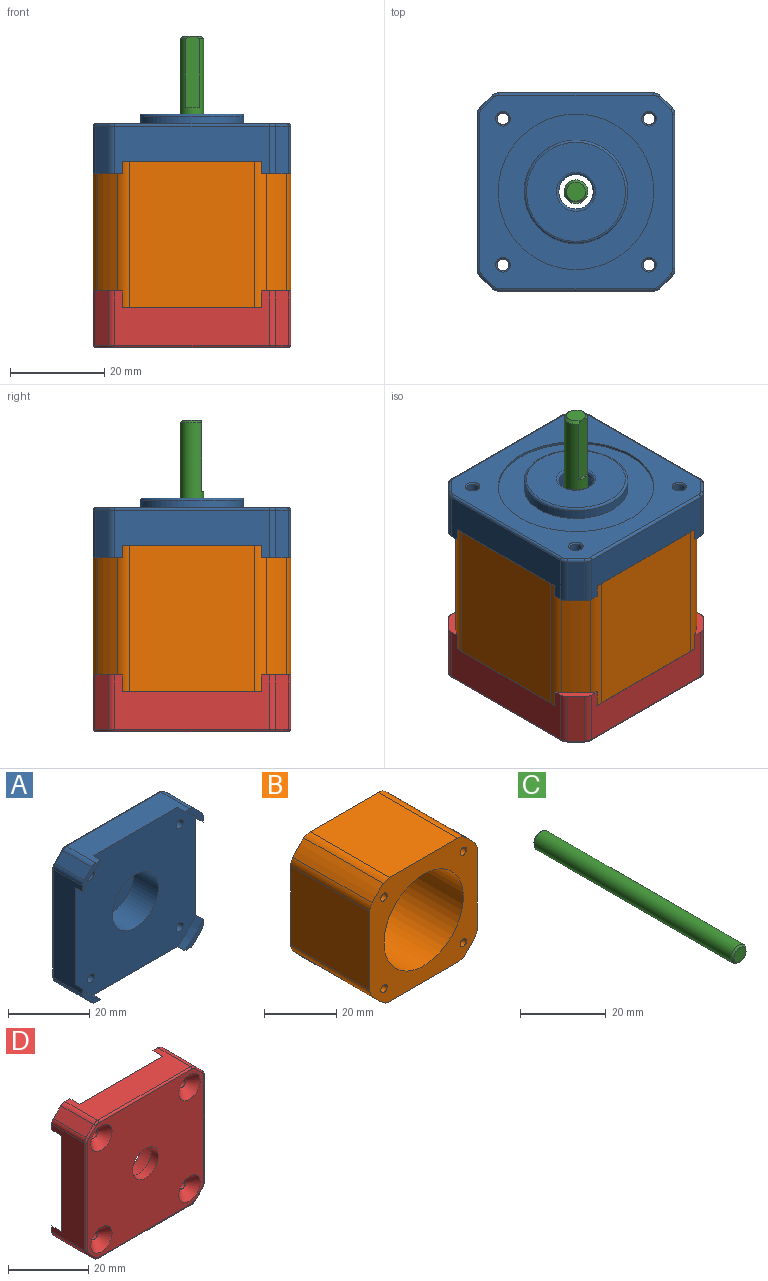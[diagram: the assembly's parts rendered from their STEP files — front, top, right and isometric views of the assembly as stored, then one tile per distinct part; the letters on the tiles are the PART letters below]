
ASSEMBLY  parts=4 mates=3
PART A: 59 faces, bbox 42.3x12.6x42.3 mm
  f0: cylinder r=3.65mm len=7.3mm, axis (0,-1,0), area 20.6mm2, adj f28,f53
  f1: plane 42x42mm, normal (0,-1,0), area 1472mm2, adj f2,f4,f6,f8,f9,f10,f11,f14
  f2: plane 32.74x10.1mm, normal (0,0,1), area 254.6mm2, adj f1,f19,f20,f21,f22,f30,f31,f51
  f3: plane 10.1x2.63mm, normal (0.71,0,0.71), area 37.5mm2, adj f22,f29,f30,f47
  f4: plane 32.74x10.1mm, normal (1,0,0), area 254.6mm2, adj f1,f21,f22,f25,f26,f29,f36,f43
  f5: plane 10.1x2.63mm, normal (0.71,0,-0.71), area 37.5mm2, adj f26,f35,f36,f39
  f6: plane 32.74x10.1mm, normal (0,0,-1), area 254.6mm2, adj f1,f23,f24,f25,f26,f34,f35,f38
  f7: plane 10.1x2.63mm, normal (-0.71,0,-0.71), area 37.5mm2, adj f24,f33,f34,f42
  f8: plane 32.74x10.1mm, normal (-1,0,0), area 254.6mm2, adj f1,f19,f20,f23,f24,f32,f33,f46
  f9: cylinder r=1.25mm len=7.7mm, axis (0,-1,0), area 60.5mm2, adj f1,f58
  f10: cylinder r=1.25mm len=7.7mm, axis (0,-1,0), area 60.5mm2, adj f1,f57
  f11: cylinder r=1.25mm len=7.7mm, axis (0,-1,0), area 60.5mm2, adj f1,f56
  f12: plane 10.1x2.63mm, normal (-0.71,0,0.71), area 37.5mm2, adj f20,f31,f32,f50
  f13: cylinder r=16.5mm len=33mm, axis (0,-1,0), area 51.8mm2, adj f15,f16
  f14: cylinder r=1.25mm len=7.7mm, axis (0,-1,0), area 60.5mm2, adj f1,f55
  f15: plane 41x41mm, normal (0,1,0), area 770.5mm2, adj f13,f37,f38,f39,f40,f41,f42,f43
  f16: plane 33x33mm, normal (0,1,0), area 475.2mm2, adj f13,f17
  f17: cylinder r=11mm len=22mm, axis (0,-1,0), area 138.2mm2, adj f16,f54
  f18: plane 21x21mm, normal (0,1,0), area 292.3mm2, adj f53,f54
  f19: cylinder r=25.6mm len=6.36mm, axis (0,1,0), area 23.5mm2, adj f1,f2,f8,f20
  f20: plane 6.36x6.36mm, normal (0,-1,0), area 10.4mm2, adj f2,f8,f12,f19,f31,f32
  f21: cylinder r=25.6mm len=6.36mm, axis (0,1,0), area 23.5mm2, adj f1,f2,f4,f22
  f22: plane 6.36x6.36mm, normal (0,-1,0), area 10.4mm2, adj f2,f3,f4,f21,f29,f30
  f23: cylinder r=25.6mm len=6.36mm, axis (0,1,0), area 23.5mm2, adj f1,f6,f8,f24
  f24: plane 6.36x6.36mm, normal (0,-1,0), area 10.4mm2, adj f6,f7,f8,f23,f33,f34
  f25: cylinder r=25.6mm len=6.36mm, axis (0,1,0), area 23.5mm2, adj f1,f4,f6,f26
  f26: plane 6.36x6.36mm, normal (0,-1,0), area 10.4mm2, adj f4,f5,f6,f25,f35,f36
  f27: cylinder r=8mm len=16mm, axis (0,-1,0), area 432.3mm2, adj f1,f28
  f28: plane 16x16mm, normal (0,-1,0), area 159.2mm2, adj f0,f27
  f29: cylinder r=2mm len=10.1mm, axis (0,-1,0), area 15.9mm2, adj f3,f4,f22,f45
  f30: cylinder r=2mm len=10.1mm, axis (0,-1,0), area 15.9mm2, adj f2,f3,f22,f49
  f31: cylinder r=2mm len=10.1mm, axis (0,-1,0), area 15.9mm2, adj f2,f12,f20,f52
  f32: cylinder r=2mm len=10.1mm, axis (0,1,0), area 15.9mm2, adj f8,f12,f20,f48
  f33: cylinder r=2mm len=10.1mm, axis (0,-1,0), area 15.9mm2, adj f7,f8,f24,f44
  f34: cylinder r=2mm len=10.1mm, axis (0,-1,0), area 15.9mm2, adj f6,f7,f24,f40
  f35: cylinder r=2mm len=10.1mm, axis (0,-1,0), area 15.9mm2, adj f5,f6,f26,f37
  f36: cylinder r=2mm len=10.1mm, axis (0,1,0), area 15.9mm2, adj f4,f5,f26,f41
  f37: torus R=1.5mm, axis (0,1,0), area 1.1mm2, adj f15,f35,f38,f39
  f38: cylinder r=0.5mm len=32.74mm, axis (1,0,0), area 25.7mm2, adj f6,f15,f37,f40
  f39: cylinder r=0.5mm len=2.98mm, axis (0.71,0,0.71), area 2.9mm2, adj f5,f15,f37,f41
  f40: torus R=1.5mm, axis (0,1,0), area 1.1mm2, adj f15,f34,f38,f42
  f41: torus R=1.5mm, axis (0,1,0), area 1.1mm2, adj f15,f36,f39,f43
  f42: cylinder r=0.5mm len=2.98mm, axis (0.71,0,-0.71), area 2.9mm2, adj f7,f15,f40,f44
  f43: cylinder r=0.5mm len=32.74mm, axis (0,0,1), area 25.7mm2, adj f4,f15,f41,f45
  f44: torus R=1.5mm, axis (0,1,0), area 1.1mm2, adj f15,f33,f42,f46
  f45: torus R=1.5mm, axis (0,1,0), area 1.1mm2, adj f15,f29,f43,f47
  f46: cylinder r=0.5mm len=32.74mm, axis (0,0,-1), area 25.7mm2, adj f8,f15,f44,f48
  f47: cylinder r=0.5mm len=2.98mm, axis (-0.71,0,0.71), area 2.9mm2, adj f3,f15,f45,f49
  f48: torus R=1.5mm, axis (0,1,0), area 1.1mm2, adj f15,f32,f46,f50
  f49: torus R=1.5mm, axis (0,1,0), area 1.1mm2, adj f15,f30,f47,f51
  f50: cylinder r=0.5mm len=2.98mm, axis (-0.71,0,-0.71), area 2.9mm2, adj f12,f15,f48,f52
  f51: cylinder r=0.5mm len=32.74mm, axis (-1,0,0), area 25.7mm2, adj f2,f15,f49,f52
  f52: torus R=1.5mm, axis (0,1,0), area 1.1mm2, adj f15,f31,f50,f51
  f53: torus R=4.15mm, axis (0,1,0), area 18.9mm2, adj f0,f18
  f54: torus R=10.5mm, axis (0,1,0), area 53.4mm2, adj f17,f18
  f55: cone r=1.25mm half-angle=45deg, axis (0,1,0), area 3.7mm2, adj f14,f15
  f56: cone r=1.25mm half-angle=45deg, axis (0,1,0), area 3.7mm2, adj f11,f15
  f57: cone r=1.25mm half-angle=45deg, axis (0,1,0), area 3.7mm2, adj f10,f15
  f58: cone r=1.25mm half-angle=45deg, axis (0,1,0), area 3.7mm2, adj f9,f15
PART B: 23 faces, bbox 42x31x42 mm
  f0: plane 42x42mm, normal (0,1,0), area 916.8mm2, adj f1,f2,f3,f4,f5,f6,f7,f8
  f1: cylinder r=25.6mm len=31mm, axis (0,-1,0), area 191.4mm2, adj f0,f16,f17,f22
  f2: plane 31x26.65mm, normal (0,0,-1), area 826.2mm2, adj f0,f15,f16,f22
  f3: cylinder r=25.6mm len=31mm, axis (0,-1,0), area 191.4mm2, adj f0,f14,f15,f22
  f4: plane 31x26.65mm, normal (-1,0,0), area 826.2mm2, adj f0,f14,f21,f22
  f5: cylinder r=25.6mm len=31mm, axis (0,-1,0), area 191.4mm2, adj f0,f20,f21,f22
  f6: plane 31x26.65mm, normal (0,0,1), area 826.2mm2, adj f0,f19,f20,f22
  f7: cylinder r=25.6mm len=31mm, axis (0,-1,0), area 191.4mm2, adj f0,f18,f19,f22
  f8: plane 31x26.65mm, normal (1,0,0), area 826.2mm2, adj f0,f17,f18,f22
  f9: cylinder r=15.5mm len=31mm, axis (0,-1,0), area 3019.1mm2, adj f0,f22
  f10: cylinder r=1.25mm len=31mm, axis (0,-1,0), area 243.5mm2, adj f0,f22
  f11: cylinder r=1.25mm len=31mm, axis (0,-1,0), area 243.5mm2, adj f0,f22
  f12: cylinder r=1.25mm len=31mm, axis (0,-1,0), area 243.5mm2, adj f0,f22
  f13: cylinder r=1.25mm len=31mm, axis (0,-1,0), area 243.5mm2, adj f0,f22
  f14: cylinder r=4mm len=31mm, axis (0,-1,0), area 82.4mm2, adj f0,f3,f4,f22
  f15: cylinder r=4mm len=31mm, axis (0,-1,0), area 82.4mm2, adj f0,f2,f3,f22
  f16: cylinder r=4mm len=31mm, axis (0,-1,0), area 82.4mm2, adj f0,f1,f2,f22
  f17: cylinder r=4mm len=31mm, axis (0,-1,0), area 82.4mm2, adj f0,f1,f8,f22
  f18: cylinder r=4mm len=31mm, axis (0,-1,0), area 82.4mm2, adj f0,f7,f8,f22
  f19: cylinder r=4mm len=31mm, axis (0,-1,0), area 82.4mm2, adj f0,f6,f7,f22
  f20: cylinder r=4mm len=31mm, axis (0,-1,0), area 82.4mm2, adj f0,f5,f6,f22
  f21: cylinder r=4mm len=31mm, axis (0,-1,0), area 82.4mm2, adj f0,f4,f5,f22
  f22: plane 42x42mm, normal (0,-1,0), area 916.8mm2, adj f1,f2,f3,f4,f5,f6,f7,f8
PART C: 7 faces, bbox 5x66x5 mm
  f0: cylinder r=2.5mm len=65mm, axis (0,-1,0), area 974.4mm2, adj f2,f3,f4,f6
  f1: plane 4x4mm, normal (0,1,0), area 12.6mm2, adj f4
  f2: plane 15x3mm, normal (0,0,-1), area 44.5mm2, adj f0,f3,f4
  f3: plane 3x0.5mm, normal (0,1,0), area 1mm2, adj f0,f2
  f4: cone r=2mm half-angle=45deg, axis (0,-1,0), area 8.6mm2, adj f0,f1,f2
  f5: plane 4x4mm, normal (0,-1,0), area 12.6mm2, adj f6
  f6: cone r=2.5mm half-angle=45deg, axis (0,1,0), area 10mm2, adj f0,f5
PART D: 53 faces, bbox 42.3x12x42.3 mm
  f0: cylinder r=4.5mm len=9mm, axis (0,-1,0), area 70.7mm2, adj f10,f28
  f1: plane 32.74x11.5mm, normal (0,0,1), area 274.1mm2, adj f9,f11,f13,f14,f16,f30,f31,f50
  f2: plane 32.74x11.5mm, normal (1,0,0), area 274.1mm2, adj f9,f11,f13,f20,f22,f29,f36,f42
  f3: plane 32.74x11.5mm, normal (0,0,-1), area 274.1mm2, adj f9,f17,f19,f20,f22,f34,f35,f39
  f4: plane 32.74x11.5mm, normal (-1,0,0), area 274.1mm2, adj f9,f14,f16,f17,f19,f32,f33,f47
  f5: cylinder r=1.25mm len=6mm, axis (0,-1,0), area 47.1mm2, adj f9,f26
  f6: cylinder r=1.25mm len=6mm, axis (0,-1,0), area 47.1mm2, adj f9,f25
  f7: cylinder r=1.25mm len=6mm, axis (0,-1,0), area 47.1mm2, adj f9,f24
  f8: cylinder r=1.25mm len=6mm, axis (0,-1,0), area 47.1mm2, adj f9,f23
  f9: plane 42x42mm, normal (0,1,0), area 1472mm2, adj f1,f2,f3,f4,f5,f6,f7,f8
  f10: plane 41x41mm, normal (0,-1,0), area 1415.7mm2, adj f0,f23,f24,f25,f26,f37,f38,f39
  f11: cylinder r=25.6mm len=6.36mm, axis (0,-1,0), area 31.6mm2, adj f1,f2,f9,f13
  f12: plane 11.5x2.63mm, normal (0.71,0,0.71), area 42.7mm2, adj f13,f29,f30,f46
  f13: plane 6.36x6.36mm, normal (0,1,0), area 10.4mm2, adj f1,f2,f11,f12,f29,f30
  f14: cylinder r=25.6mm len=6.36mm, axis (0,-1,0), area 31.6mm2, adj f1,f4,f9,f16
  f15: plane 11.5x2.63mm, normal (-0.71,0,0.71), area 42.7mm2, adj f16,f31,f32,f51
  f16: plane 6.36x6.36mm, normal (0,1,0), area 10.4mm2, adj f1,f4,f14,f15,f31,f32
  f17: cylinder r=25.6mm len=6.36mm, axis (0,-1,0), area 31.6mm2, adj f3,f4,f9,f19
  f18: plane 11.5x2.63mm, normal (-0.71,0,-0.71), area 42.7mm2, adj f19,f33,f34,f43
  f19: plane 6.36x6.36mm, normal (0,1,0), area 10.4mm2, adj f3,f4,f17,f18,f33,f34
  f20: cylinder r=25.6mm len=6.36mm, axis (0,-1,0), area 31.6mm2, adj f2,f3,f9,f22
  f21: plane 11.5x2.63mm, normal (0.71,0,-0.71), area 42.7mm2, adj f22,f35,f36,f38
  f22: plane 6.36x6.36mm, normal (0,1,0), area 10.4mm2, adj f2,f3,f20,f21,f35,f36
  f23: cone r=3.75mm half-angle=45deg, axis (0,-1,0), area 55.5mm2, adj f8,f10
  f24: cone r=3.75mm half-angle=45deg, axis (0,-1,0), area 55.5mm2, adj f7,f10
  f25: cone r=3.75mm half-angle=45deg, axis (0,-1,0), area 55.5mm2, adj f6,f10
  f26: cone r=3.75mm half-angle=45deg, axis (0,-1,0), area 55.5mm2, adj f5,f10
  f27: cylinder r=8mm len=16mm, axis (0,1,0), area 301.6mm2, adj f9,f28
  f28: plane 16x16mm, normal (0,1,0), area 137.4mm2, adj f0,f27
  f29: cylinder r=2mm len=11.5mm, axis (0,-1,0), area 18.1mm2, adj f2,f12,f13,f44
  f30: cylinder r=2mm len=11.5mm, axis (0,-1,0), area 18.1mm2, adj f1,f12,f13,f48
  f31: cylinder r=2mm len=11.5mm, axis (0,-1,0), area 18.1mm2, adj f1,f15,f16,f52
  f32: cylinder r=2mm len=11.5mm, axis (0,1,0), area 18.1mm2, adj f4,f15,f16,f49
  f33: cylinder r=2mm len=11.5mm, axis (0,-1,0), area 18.1mm2, adj f4,f18,f19,f45
  f34: cylinder r=2mm len=11.5mm, axis (0,-1,0), area 18.1mm2, adj f3,f18,f19,f41
  f35: cylinder r=2mm len=11.5mm, axis (0,-1,0), area 18.1mm2, adj f3,f21,f22,f37
  f36: cylinder r=2mm len=11.5mm, axis (0,1,0), area 18.1mm2, adj f2,f21,f22,f40
  f37: torus R=1.5mm, axis (0,1,0), area 1.1mm2, adj f10,f35,f38,f39
  f38: cylinder r=0.5mm len=2.98mm, axis (-0.71,0,-0.71), area 2.9mm2, adj f10,f21,f37,f40
  f39: cylinder r=0.5mm len=32.74mm, axis (-1,0,0), area 25.7mm2, adj f3,f10,f37,f41
  f40: torus R=1.5mm, axis (0,1,0), area 1.1mm2, adj f10,f36,f38,f42
  f41: torus R=1.5mm, axis (0,1,0), area 1.1mm2, adj f10,f34,f39,f43
  f42: cylinder r=0.5mm len=32.74mm, axis (0,0,-1), area 25.7mm2, adj f2,f10,f40,f44
  f43: cylinder r=0.5mm len=2.98mm, axis (-0.71,0,0.71), area 2.9mm2, adj f10,f18,f41,f45
  f44: torus R=1.5mm, axis (0,1,0), area 1.1mm2, adj f10,f29,f42,f46
  f45: torus R=1.5mm, axis (0,1,0), area 1.1mm2, adj f10,f33,f43,f47
  f46: cylinder r=0.5mm len=2.98mm, axis (0.71,0,-0.71), area 2.9mm2, adj f10,f12,f44,f48
  f47: cylinder r=0.5mm len=32.74mm, axis (0,0,1), area 25.7mm2, adj f4,f10,f45,f49
  f48: torus R=1.5mm, axis (0,1,0), area 1.1mm2, adj f10,f30,f46,f50
  f49: torus R=1.5mm, axis (0,1,0), area 1.1mm2, adj f10,f32,f47,f51
  f50: cylinder r=0.5mm len=32.74mm, axis (1,0,0), area 25.7mm2, adj f1,f10,f48,f52
  f51: cylinder r=0.5mm len=2.98mm, axis (0.71,0,0.71), area 2.9mm2, adj f10,f15,f49,f52
  f52: torus R=1.5mm, axis (0,1,0), area 1.1mm2, adj f10,f31,f50,f51
PLACE A rot(axis=(1,0,0),90deg) t=(-59.47,-14.57,31.4)mm
PLACE B rot(axis=(1,0,0),90deg) t=(-59.47,-14.57,15.4)mm
PLACE C rot(axis=(0.01,-0.71,-0.71),178.4deg) t=(-59.47,-14.57,-8.1)mm
PLACE D rot(axis=(1,0,0),90deg) t=(-59.47,-14.57,-8.1)mm fixed
MATE revolute C.f0 <-> D.f0  axis (0,0,1) through (-59.47,-14.57,-8.1)mm
MATE fastened A.f27 <-> B.f1  axis (0,0,-1) through (-59.47,-14.57,31.4)mm
MATE fastened D.f0 <-> B.f1  axis (0,0,1) through (-59.47,-14.57,0.4)mm
